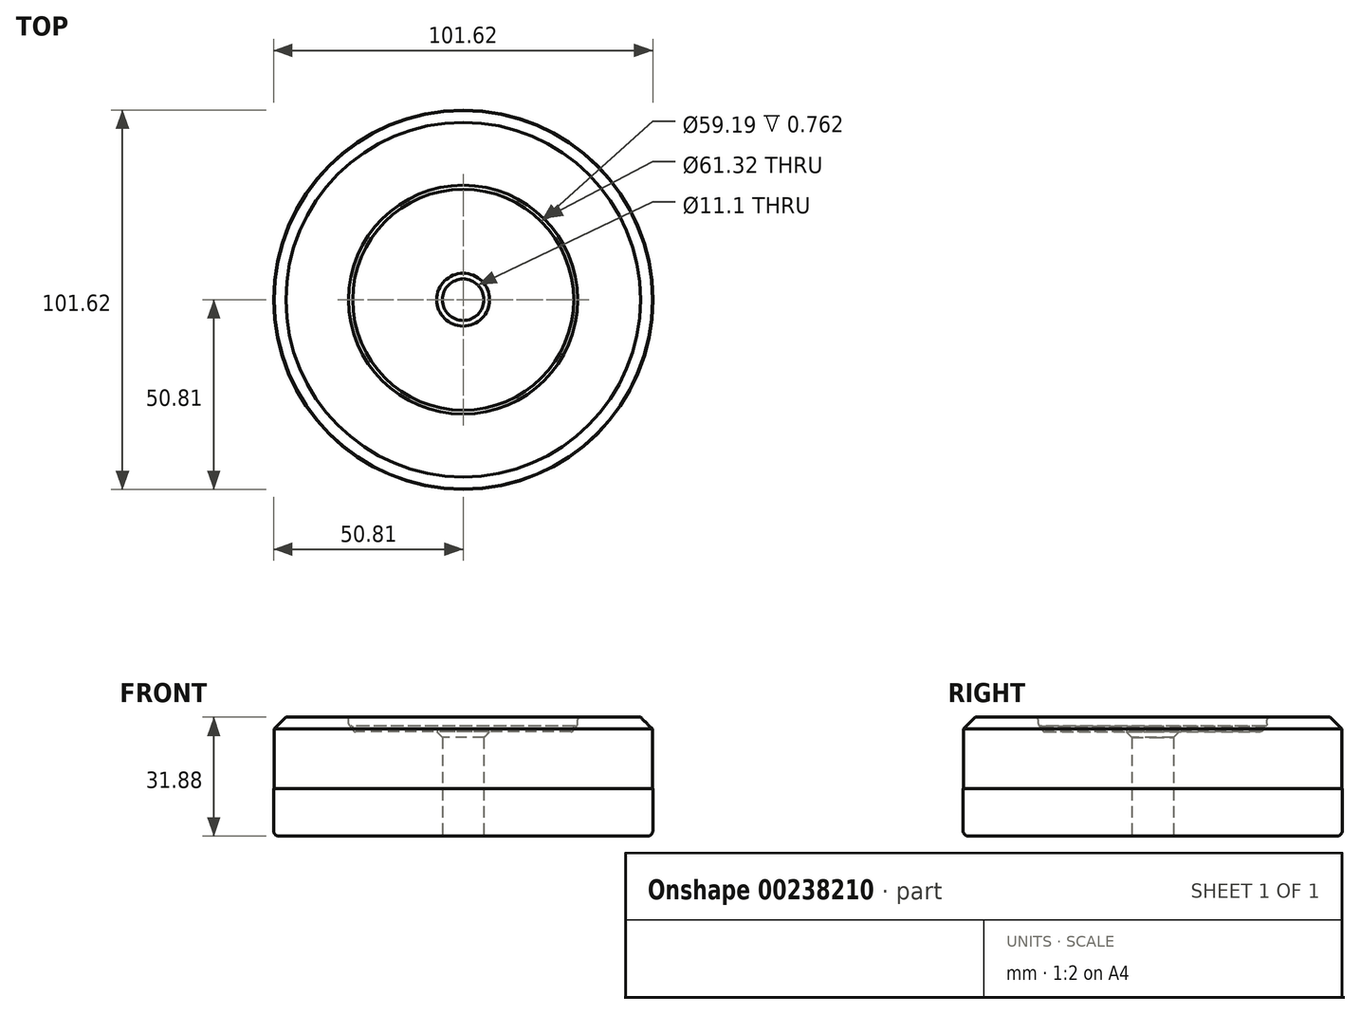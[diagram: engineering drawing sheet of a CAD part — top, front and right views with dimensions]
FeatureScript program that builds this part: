
annotation { "Feature Type Name" : "Feature", "Feature Type Description" : "" }
export const myFeature = defineFeature(function(context is Context, id is Id, definition is map)
    precondition{}
    {
        {
            var Q0;
            Q0=qCreatedBy(makeId("Front.planeOp"),FACE);
            var sketch = newSketch(context, id + "F0", { "sketchPlane" : qUnion([Q0])});
            skLineSegment(sketch, "E0", {"start": v(0, 0) * mm, "end": v(-50.8, 0) * mm});
            skLineSegment(sketch, "E1", {"start": v(-50.8, 0) * mm, "end": v(-50.8, 12.7) * mm});
            skLineSegment(sketch, "E2", {"start": v(-47.5, 31.88) * mm, "end": v(-31.42, 31.88) * mm});
            skLineSegment(sketch, "E3", {"start": v(0, 27.94) * mm, "end": v(0, 0) * mm});
            skLineSegment(sketch, "E4", {"start": v(0, 27.94) * mm, "end": v(-28.83, 27.94) * mm});
            skLineSegment(sketch, "E5", {"start": v(-29.6, 28.7) * mm, "end": v(-29.6, 29.46) * mm});
            skLineSegment(sketch, "E6", {"start": v(-29.6, 29.46) * mm, "end": v(-30.05, 29.46) * mm});
            skLineSegment(sketch, "E7", {"start": v(-30.66, 30.07) * mm, "end": v(-30.66, 31.11) * mm});
            skPoint(sketch, "E8.orphan", {"position": v(0, 31.88) * mm});
            skPoint(sketch, "E9.visualSharp", {"position": v(-29.6, 27.94) * mm});
            skArc(sketch, "E9.filletArc", {"start": v(-29.6, 28.7) * mm, "mid": v(-29.37, 28.16) * mm, "end": v(-28.83, 27.94) * mm});
            skPoint(sketch, "E10.visualSharp", {"position": v(-30.66, 29.46) * mm});
            skArc(sketch, "E10.filletArc", {"start": v(-30.66, 30.07) * mm, "mid": v(-30.48, 29.64) * mm, "end": v(-30.05, 29.46) * mm});
            skPoint(sketch, "E11.visualSharp", {"position": v(-30.66, 31.88) * mm});
            skArc(sketch, "E11.filletArc", {"start": v(-30.66, 31.11) * mm, "mid": v(-30.88, 31.65) * mm, "end": v(-31.42, 31.88) * mm});
            skLineSegment(sketch, "E12", {"start": v(-50.68, 28.7) * mm, "end": v(-47.5, 31.88) * mm});
            skPoint(sketch, "E13.orphan", {"position": v(-50.8, 31.88) * mm});
            skLineSegment(sketch, "E14", {"start": v(-50.68, 28.7) * mm, "end": v(-50.68, 12.7) * mm});
            skLineSegment(sketch, "E15", {"start": v(-50.68, 12.7) * mm, "end": v(-50.8, 12.7) * mm});
            skPoint(sketch, "E16.orphan", {"position": v(-50.8, 28.57) * mm});
            skSolve(sketch);
        }
        {
            var Q0;
            Q0 = qSketchRegion(id + "F0", true);
            var Q1;
            Q1=sQuery(id+"F0.wireOp",EDGE,"E3");
            revolve(context, id + "F1", {"entities" : qUnion([Q0]), "axis" : qUnion([Q1]), "revolveType" : RevolveType.FULL});
        }
        {
            var Q0;
            Q0=qCreatedBy(makeId("Top.planeOp"),FACE);
            var sketch = newSketch(context, id + "F2", { "sketchPlane" : qUnion([Q0])});
            skCircle(sketch, "E17", {"center": v(0, 0) * mm, "radius": 5.55 * mm});
            skSolve(sketch);
        }
        {
            var Q0;
            Q0 = qSketchRegion(id + "F2", true);
            extrude(context, id + "F3", {"entities" : qUnion([Q0]), "operationType" : NewBodyOperationType.REMOVE, "endBound" : BoundingType.THROUGH_ALL, "depth" : 25.4 * mm});
        }
        {
            var Q0;
            Q0=makeQuery(id+"F3.boolean.opBoolean","INTERSECT",EDGE,{"derivedFrom":[makeQuery(id+"F1.opRevolve","SWEPT_FACE",FACE,{"disambiguationData":[OSD([sQuery(id+"F0.wireOp",EDGE,"E4")])]}),makeQuery(id+"F3.opExtrude","SWEPT_FACE",FACE,{"disambiguationData":[OSD([sQuery(id+"F2.wireOp",EDGE,"E17")])]})]});
            var Q1;
            Q1=makeQuery(id+"F3.boolean.opBoolean","COPY",EDGE,{"derivedFrom":makeQuery(id+"F3.opExtrude","CAP_EDGE",EDGE,{"disambiguationData":[OSD([sQuery(id+"F2.wireOp",EDGE,"E17")])],"isStart":true})});
            chamfer(context, id + "F4", {"entities" : qUnion([Q0, Q1]), "width" : 1.52 * mm, "tangentPropagation" : true});
        }
        {
            var Q0;
            Q0=makeQuery(id+"F1.opRevolve","SWEPT_EDGE",EDGE,{"disambiguationData":[OSD([sQuery(id+"F0.wireOp",EDGE,"E0"),sQuery(id+"F0.wireOp",EDGE,"E1")])]});
            fillet(context, id + "F5", {"entities" : qUnion([Q0]), "radius" : 1.52 * mm, "tangentPropagation" : true, "allowEdgeOverflow" : false});
        }
    });
